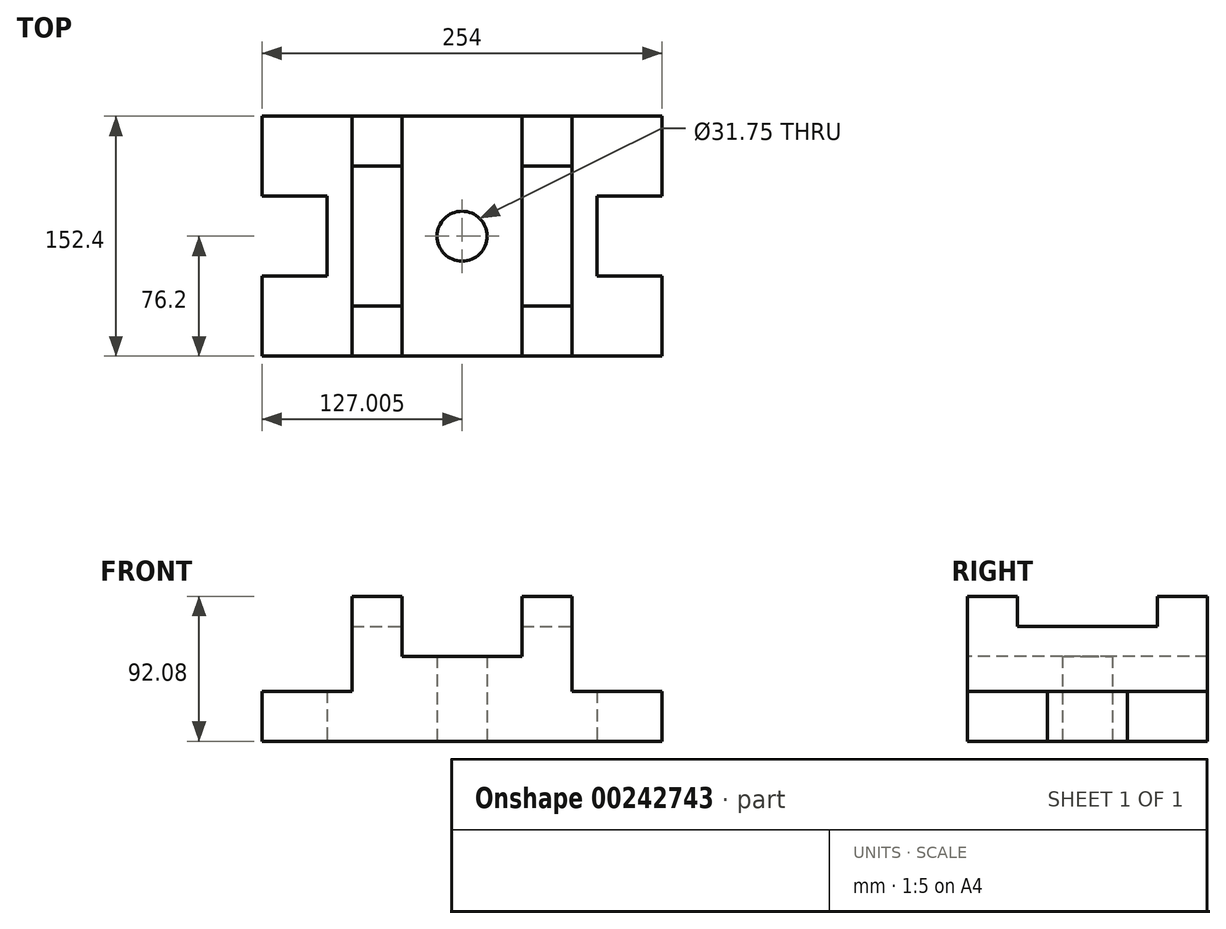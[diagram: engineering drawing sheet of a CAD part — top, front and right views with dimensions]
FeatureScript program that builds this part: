
annotation { "Feature Type Name" : "Feature", "Feature Type Description" : "" }
export const myFeature = defineFeature(function(context is Context, id is Id, definition is map)
    precondition{}
    {
        {
            var Q0;
            Q0=qCreatedBy(makeId("Top.planeOp"),FACE);
            var sketch = newSketch(context, id + "F0", { "sketchPlane" : qUnion([Q0])});
            skLineSegment(sketch, "E0.bottom", {"start": v(-119, 101.6) * mm, "end": v(135, 101.6) * mm});
            skLineSegment(sketch, "E0.top", {"start": v(-119, -50.8) * mm, "end": v(135, -50.8) * mm});
            skLineSegment(sketch, "E0.left", {"start": v(-119, 101.6) * mm, "end": v(-119, 50.8) * mm});
            skLineSegment(sketch, "E0.right", {"start": v(135, 101.6) * mm, "end": v(135, 50.8) * mm});
            skLineSegment(sketch, "E1", {"start": v(-119, 0) * mm, "end": v(-77.72, 0) * mm});
            skLineSegment(sketch, "E2", {"start": v(-77.72, 0) * mm, "end": v(-77.72, 50.8) * mm});
            skLineSegment(sketch, "E3", {"start": v(-77.72, 50.8) * mm, "end": v(-119, 50.8) * mm});
            skLineSegment(sketch, "E4", {"start": v(135, 50.8) * mm, "end": v(93.73, 50.8) * mm});
            skLineSegment(sketch, "E5", {"start": v(93.73, 50.8) * mm, "end": v(93.73, 0) * mm});
            skLineSegment(sketch, "E6", {"start": v(93.73, 0) * mm, "end": v(135, 0) * mm});
            skLineSegment(sketch, "E7", {"start": v(77.85, 101.6) * mm, "end": v(77.85, -50.8) * mm});
            skLineSegment(sketch, "E8", {"start": v(46.1, 101.6) * mm, "end": v(46.1, -50.8) * mm});
            skLineSegment(sketch, "E9", {"start": v(46.1, -19.05) * mm, "end": v(77.85, -19.05) * mm});
            skLineSegment(sketch, "E10", {"start": v(46.1, 69.85) * mm, "end": v(77.85, 69.85) * mm});
            skLineSegment(sketch, "E11", {"start": v(-61.85, 101.6) * mm, "end": v(-61.85, -50.8) * mm});
            skLineSegment(sketch, "E12", {"start": v(-30.1, 101.6) * mm, "end": v(-30.1, -50.8) * mm});
            skLineSegment(sketch, "E13", {"start": v(-61.85, 69.85) * mm, "end": v(-30.1, 69.85) * mm});
            skLineSegment(sketch, "E14", {"start": v(-61.85, -19.05) * mm, "end": v(-30.1, -19.05) * mm});
            skLineSegment(sketch, "E15.trimOffspring", {"start": v(135, 0) * mm, "end": v(135, -50.8) * mm});
            skLineSegment(sketch, "E16.trimOffspring", {"start": v(-119, 0) * mm, "end": v(-119, -50.8) * mm});
            skPoint(sketch, "E17.positionSnap0", {"position": v(46.1, 25.4) * mm});
            skCircle(sketch, "E18", {"center": v(8, 25.4) * mm, "radius": 15.88 * mm});
            skSolve(sketch);
        }
        {
            var Q0;
            {var subQ4=sQuery(id+"F0.wireOp",EDGE,"E0.left");Q0=makeQuery(id+"F0.imprint","IMPRINT",FACE,{"disambiguationData":[TD([[makeQuery(id+"F0.imprint","IMPRINT",EDGE,{"derivedFrom":subQ4}),1.0]])]});}
            var Q1;
            {var subQ0=sQuery(id+"F0.wireOp",EDGE,"E0.right");Q1=makeQuery(id+"F0.imprint","IMPRINT",FACE,{"disambiguationData":[TD([[makeQuery(id+"F0.imprint","IMPRINT",EDGE,{"derivedFrom":subQ0}),-1.0]])]});}
            extrude(context, id + "F1", {"entities" : qUnion([Q0, Q1]), "depth" : 31.75 * mm});
        }
        {
            var Q0;
            {var subQ5=sQuery(id+"F0.wireOp",EDGE,"E13");Q0=makeQuery(id+"F0.imprint","IMPRINT",FACE,{"disambiguationData":[TD([[makeQuery(id+"F0.imprint","IMPRINT",EDGE,{"derivedFrom":subQ5}),1.0]])]});}
            var Q1;
            {var subQ5=sQuery(id+"F0.wireOp",EDGE,"E10");Q1=makeQuery(id+"F0.imprint","IMPRINT",FACE,{"disambiguationData":[TD([[makeQuery(id+"F0.imprint","IMPRINT",EDGE,{"derivedFrom":subQ5}),1.0]])]});}
            var Q2;
            {var subQ5=sQuery(id+"F0.wireOp",EDGE,"E14");Q2=makeQuery(id+"F0.imprint","IMPRINT",FACE,{"disambiguationData":[TD([[makeQuery(id+"F0.imprint","IMPRINT",EDGE,{"derivedFrom":subQ5}),-1.0]])]});}
            var Q3;
            {var subQ5=sQuery(id+"F0.wireOp",EDGE,"E9");Q3=makeQuery(id+"F0.imprint","IMPRINT",FACE,{"disambiguationData":[TD([[makeQuery(id+"F0.imprint","IMPRINT",EDGE,{"derivedFrom":subQ5}),-1.0]])]});}
            extrude(context, id + "F2", {"entities" : qUnion([Q0, Q1, Q2, Q3]), "operationType" : NewBodyOperationType.ADD, "depth" : 92.07 * mm});
        }
        {
            var Q0;
            {var subQ0=sQuery(id+"F0.wireOp",EDGE,"E9");Q0=makeQuery(id+"F0.imprint","IMPRINT",FACE,{"disambiguationData":[TD([[makeQuery(id+"F0.imprint","IMPRINT",EDGE,{"derivedFrom":subQ0}),1.0]])]});}
            var Q1;
            {var subQ0=sQuery(id+"F0.wireOp",EDGE,"E13");Q1=makeQuery(id+"F0.imprint","IMPRINT",FACE,{"disambiguationData":[TD([[makeQuery(id+"F0.imprint","IMPRINT",EDGE,{"derivedFrom":subQ0}),-1.0]])]});}
            extrude(context, id + "F3", {"entities" : qUnion([Q0, Q1]), "operationType" : NewBodyOperationType.ADD, "depth" : 73.02 * mm});
        }
        {
            var Q0;
            Q0=makeQuery(id+"F0.imprint","IMPRINT",FACE,{"disambiguationData":[TD([[makeQuery(id+"F0.imprint","IMPRINT",EDGE,{"derivedFrom":sQuery(id+"F0.wireOp",EDGE,"E18")}),-1.0]])]});
            extrude(context, id + "F4", {"entities" : qUnion([Q0]), "operationType" : NewBodyOperationType.ADD, "depth" : 53.97 * mm});
        }
    });
